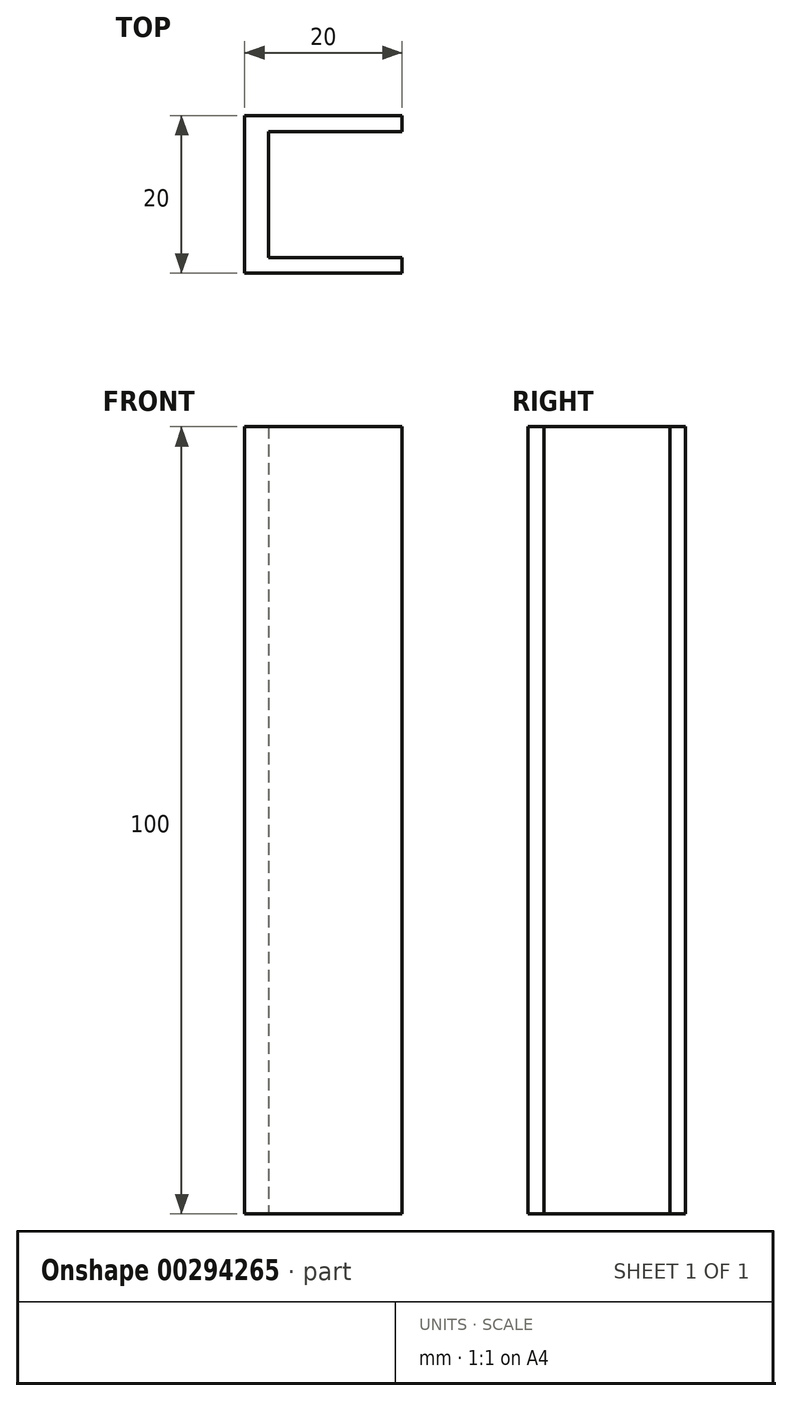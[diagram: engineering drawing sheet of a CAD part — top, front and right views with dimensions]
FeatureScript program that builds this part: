
annotation { "Feature Type Name" : "Feature", "Feature Type Description" : "" }
export const myFeature = defineFeature(function(context is Context, id is Id, definition is map)
    precondition{}
    {
        {
            var Q0;
            Q0=qCreatedBy(makeId("Top.planeOp"),FACE);
            var sketch = newSketch(context, id + "F0", { "sketchPlane" : qUnion([Q0])});
            skLineSegment(sketch, "E0", {"start": v(0, 20) * mm, "end": v(-20, 20) * mm});
            skLineSegment(sketch, "E1", {"start": v(-20, 20) * mm, "end": v(-20, 0) * mm});
            skLineSegment(sketch, "E2", {"start": v(-20, 0) * mm, "end": v(0, 0) * mm});
            skLineSegment(sketch, "E3", {"start": v(0, 0) * mm, "end": v(0, 2) * mm});
            skLineSegment(sketch, "E4", {"start": v(0, 2) * mm, "end": v(-17, 2) * mm});
            skLineSegment(sketch, "E5", {"start": v(-17, 2) * mm, "end": v(-17, 18) * mm});
            skLineSegment(sketch, "E6", {"start": v(-17, 18) * mm, "end": v(0, 18) * mm});
            skLineSegment(sketch, "E7", {"start": v(0, 20) * mm, "end": v(0, 18) * mm});
            skSolve(sketch);
        }
        {
            var Q0;
            Q0 = qSketchRegion(id + "F0", true);
            extrude(context, id + "F1", {"entities" : qUnion([Q0]), "depth" : 100 * mm});
        }
    });
